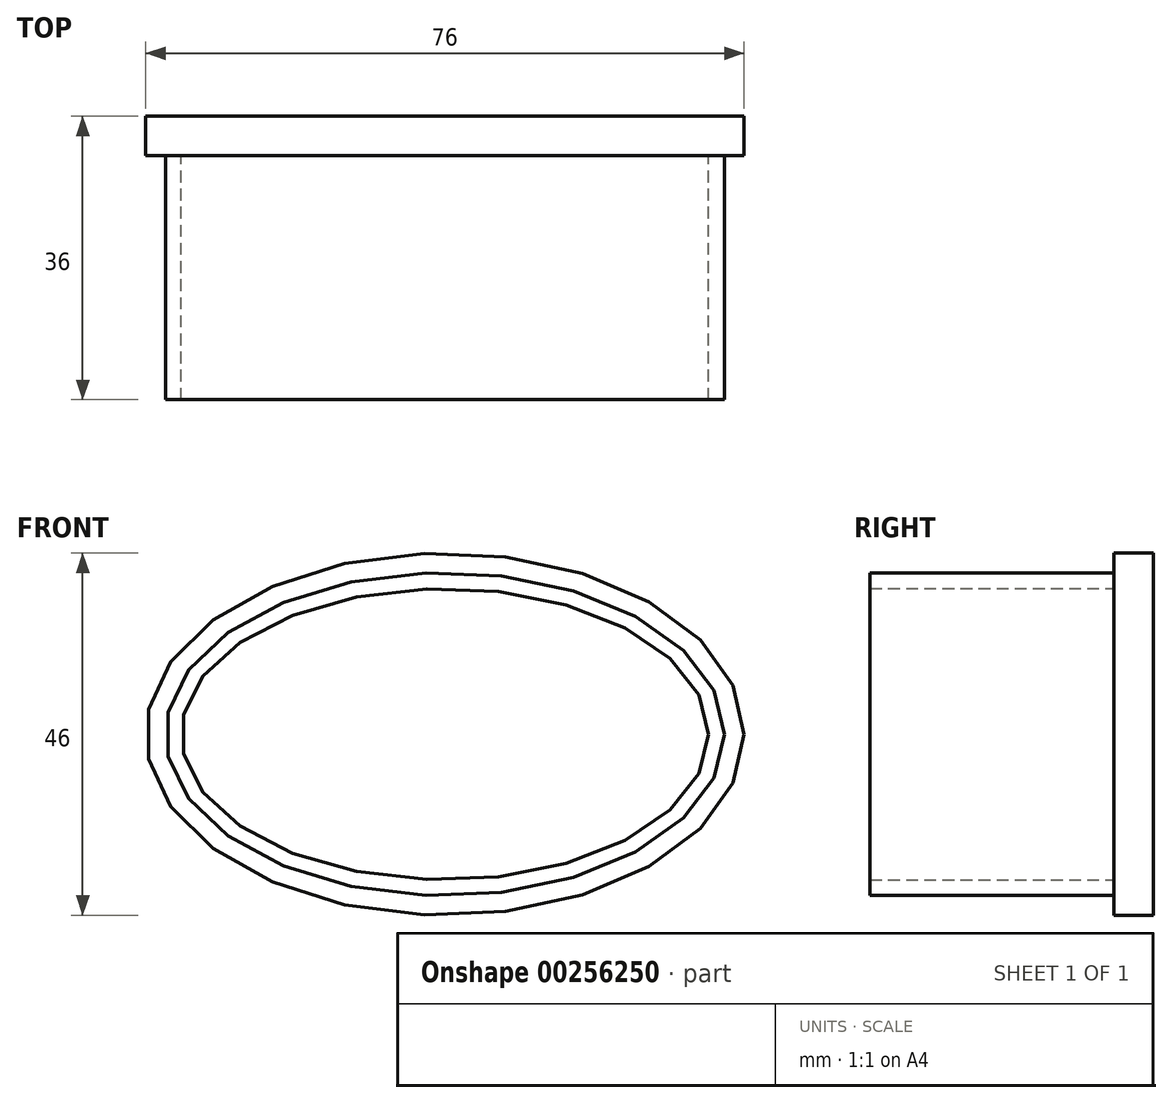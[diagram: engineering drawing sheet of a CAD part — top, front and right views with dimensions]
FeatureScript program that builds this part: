
annotation { "Feature Type Name" : "Feature", "Feature Type Description" : "" }
export const myFeature = defineFeature(function(context is Context, id is Id, definition is map)
    precondition{}
    {
        {
            var Q0;
            Q0=qCreatedBy(makeId("Front.planeOp"),FACE);
            var sketch = newSketch(context, id + "F0", { "sketchPlane" : qUnion([Q0])});
            skEllipse(sketch, "E0", {"center": v(0, 0) * mm, "majorRadius": 35.5 * mm, "minorRadius": 20.5 * mm, "majorAxis": v(1, 0)});
            skEllipse(sketch, "E1", {"center": v(0, 0) * mm, "majorRadius": 33.5 * mm, "minorRadius": 18.5 * mm, "majorAxis": v(1, 0)});
            skSolve(sketch);
        }
        {
            var Q0;
            Q0=makeQuery(id+"F0.imprint","IMPRINT",FACE,{"disambiguationData":[TD([[makeQuery(id+"F0.imprint","IMPRINT",EDGE,{"derivedFrom":sQuery(id+"F0.wireOp",EDGE,"E0")}),1.0]])]});
            extrude(context, id + "F1", {"entities" : qUnion([Q0]), "depth" : 31 * mm});
        }
        {
            var Q0;
            Q0=qCreatedBy(makeId("Front.planeOp"),FACE);
            var sketch = newSketch(context, id + "F2", { "sketchPlane" : qUnion([Q0])});
            skEllipse(sketch, "E2", {"center": v(0, 0) * mm, "majorRadius": 38 * mm, "minorRadius": 23 * mm, "majorAxis": v(1, 0)});
            skSolve(sketch);
        }
        {
            var Q0;
            Q0=makeQuery(id+"F2.imprint","IMPRINT",FACE,{"disambiguationData":[TD([[makeQuery(id+"F2.imprint","IMPRINT",EDGE,{"derivedFrom":sQuery(id+"F2.wireOp",EDGE,"E2")}),1.0]])]});
            extrude(context, id + "F3", {"entities" : qUnion([Q0]), "operationType" : NewBodyOperationType.ADD, "oppositeDirection" : true, "depth" : 5 * mm});
        }
    });
